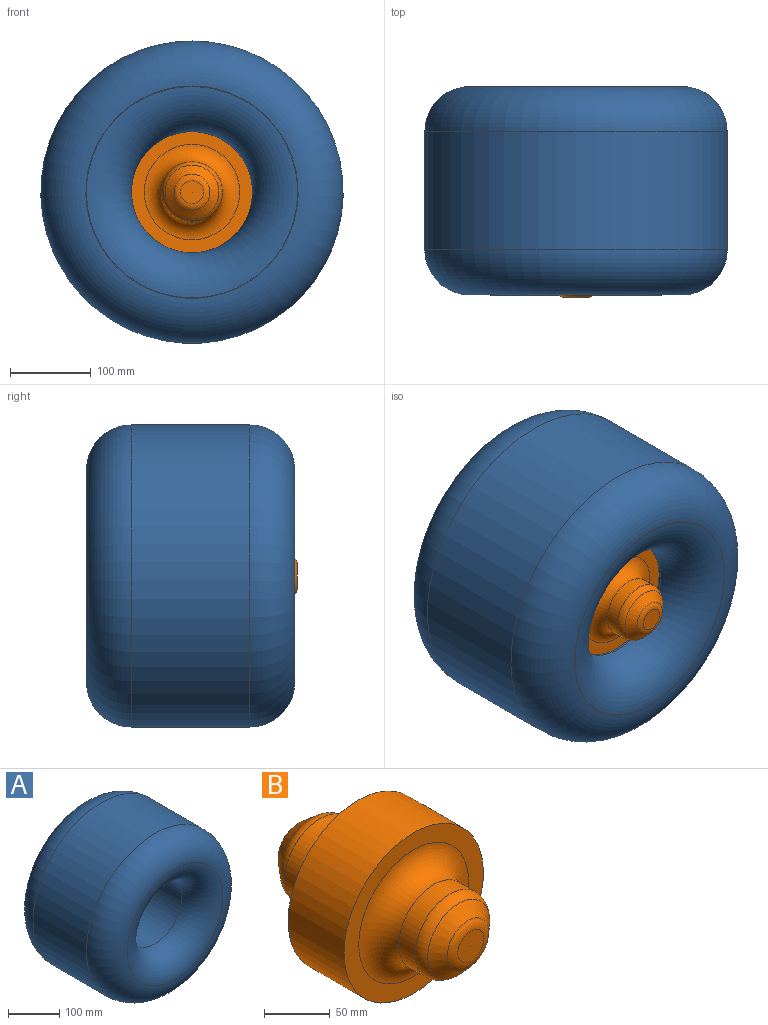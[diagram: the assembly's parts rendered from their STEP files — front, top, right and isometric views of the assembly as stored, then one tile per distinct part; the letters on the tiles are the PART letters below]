
ASSEMBLY  parts=2 mates=1
PART A: 8 faces, bbox 406.2x258.5x406.2 mm
  f0: plane 263.49x263.49mm, normal (0,-1,0), area 550.1mm2, adj f4,f7
  f1: cylinder r=75.18mm len=150.36mm, axis (0,-1,0), area 69281.5mm2, adj f4,f5
  f2: plane 263.49x263.49mm, normal (0,1,0), area 550.1mm2, adj f5,f6
  f3: cylinder r=187.64mm len=375.28mm, axis (0,-1,0), area 172916.2mm2, adj f6,f7
  f4: torus R=131.08mm, axis (0,1,0), area 52681.9mm2, adj f0,f1
  f5: torus R=131.08mm, axis (0,1,0), area 52681.9mm2, adj f1,f2
  f6: torus R=131.74mm, axis (0,1,0), area 92312.7mm2, adj f2,f3
  f7: torus R=131.74mm, axis (0,1,0), area 92312.7mm2, adj f0,f3
PART B: 15 faces, bbox 161.6x189.8x161.6 mm
  f0: plane 26.03x26.03mm, normal (0,1,0), area 531.9mm2, adj f9
  f1: cone r=18.8mm half-angle=40.5deg, axis (0,-1,0), area 3321.7mm2, adj f9,f10
  f2: cylinder r=37.59mm len=75.18mm, axis (0,-1,0), area 4568.2mm2, adj f10,f13
  f3: plane 150.36x150.36mm, normal (0,1,0), area 6725.2mm2, adj f4,f13
  f4: cylinder r=75.18mm len=150.36mm, axis (0,-1,0), area 28491.2mm2, adj f3,f5
  f5: plane 150.36x150.36mm, normal (0,-1,0), area 6725.2mm2, adj f4,f14
  f6: cylinder r=37.59mm len=75.18mm, axis (0,-1,0), area 4163.1mm2, adj f11,f14
  f7: cone r=37.59mm half-angle=48.2deg, axis (0,1,0), area 2599.5mm2, adj f11,f12
  f8: cone r=18.8mm half-angle=89.6deg, axis (0,1,0), area 621.2mm2, adj f12
  f9: torus R=13.01mm, axis (0,-1,0), area 1232.8mm2, adj f0,f1
  f10: torus R=25.04mm, axis (0,1,0), area 2040.2mm2, adj f1,f2
  f11: torus R=25.04mm, axis (0,1,0), area 2400.6mm2, adj f6,f7
  f12: torus R=13.96mm, axis (0,1,0), area 1046mm2, adj f7,f8
  f13: torus R=59.26mm, axis (0,1,0), area 9722.6mm2, adj f2,f3
  f14: torus R=59.26mm, axis (0,1,0), area 9722.6mm2, adj f5,f6
PLACE A t=(387.91,0,-12.65)mm
PLACE B t=(387.91,-38.53,-12.65)mm
MATE fastened B.f1 <-> A.f1  axis (0,-1,0) through (387.91,-128.2,-12.65)mm
